# Revit family: Flush_Valve-Toilet-American_Standard-Ultima-6047_Series
name_source: partatom
category: Plumbing Fixtures
units: mm (PartAtom-declared; Revit-internal decimal feet)

## family parameters
Always vertical = No
Cut with Voids When Loaded = No
OmniClass Number = 23.65.70.00
OmniClass Title = Terminals for Supplied Liquids and Gases
Part Type = Normal
Room Calculation Point = No
Round Connector Dimension = Use Radius
Shared = Yes
Work Plane-Based = Yes

## types (3) — shared parameters
ADA Compliant = Yes
Assembly Code = D2020300
CW Connection = Yes
CWFU = 5
CalGreen Compliant = Yes
Cold Water Connection Diameter = 1"
Cold Water Connection Height = 11 1/2"
Cold Water Connection Radius = 1/2"
Cold Water Connection Width = 4 1/4"
Cold Water Connection Width Constraint = 4 1/4"
Default Elevation = 0"
Finish = Metal-American Standard-002-Polished Chrome
Flow Rates = 25gpm (94.6 L/min.)
HW Connection = No
Height = 13 1/2"
Installation Type = Surface Mounted
Length = 3"
Manufacturer = American Standard
Material = Metal-American Standard-002-Polished Chrome
Operating Pressure = 25 psi (flowing)-80 psi (static)
Price = Prices may vary. Please consult Manufacturer Representative for most up-to-date price list.
Product Documentation Link = https://americanstandard.box.com
Product Page URL = https://www.americanstandard-us.com
Revised Date = 03/21/2022
URL = http://www.americanstandard-us.com
Valve to Wall Distance = 1 1/2"
Valve to Wall Distance Constraint = 1 1/2"
Vent Connection = No
WFU = 5
Warranty Information = 1 Year Limited Warranty
Waste Connection = No
Width = 5 1/4"
zero-valued in all types: HWFU

## per-type parameters (varying)
| type | Description | Flush Rate | IAPMO Compliance | Type Comments |
| 6047161.002 | Exposed Manual Top Spud Toilet 1.6 gpf Flush Valve for 11-1/2" Supply C\L to top of bowl | 1.6 gpf / 6.0 Lpf | ANSI/ASME A112.19.2,  ASSE 1037 | Flush Valve for 11-1/2" Supply C\L to top of bowl, 1.6 gpf / 6.0 Lpf |
| 6047121.002 | Exposed Manual Top Spud Toilet 1.28 gpf Flush Valve for 11-1/2" Supply C\L to top of bowl 1.28gpf | 1.28 gpf / 4.8 Lpf | ANSI/ASME A112.19.2,  ASSE 1037, Watersense | Flush Valve for 11-1/2" Supply C\L to top of bowl, 1.28 gpf / 4.8 Lpf
for most plumbing fixtures. |
| 6047111.002 | Ultima™ Manual Toilet Flush Valve, Piston-Type, 1.1 gpf/4.2 Lpf | 1.1 gpf / 4.2 Lpf | ANSI/ASME A112.19.2,  ASSE 1037, Watersense | Flush Valve for 11-1/2" Supply C\L to top of bowl, 1.1 gpf / 4.2 Lpf |

note: column(s) folded — value = type name in every type: Model

## geometry (parser evidence)
native form markers: Sweep x2
no freeform markers — native parametric forms only
